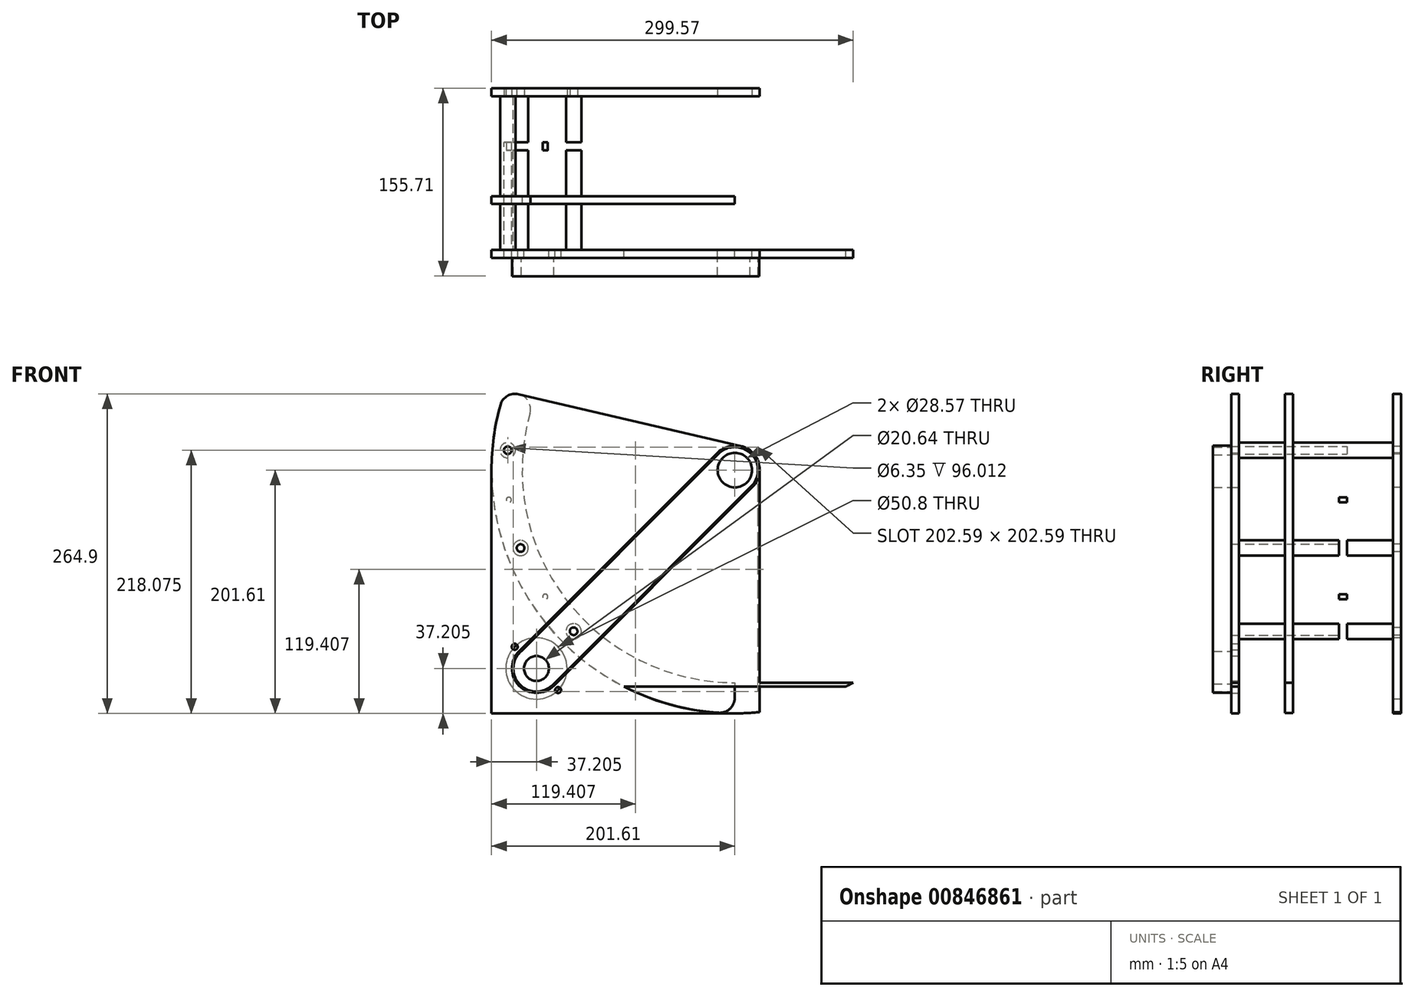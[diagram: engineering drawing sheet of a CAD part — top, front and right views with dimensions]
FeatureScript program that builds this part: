
annotation { "Feature Type Name" : "Feature", "Feature Type Description" : "" }
export const myFeature = defineFeature(function(context is Context, id is Id, definition is map)
    precondition{}
    {
        {
            var Q0;
            Q0=qCreatedBy(makeId("Front.planeOp"),FACE);
            var sketch = newSketch(context, id + "F0", { "sketchPlane" : qUnion([Q0])});
            skCircle(sketch, "E0", {"center": v(0, 0) * mm, "radius": 61.91 * mm});
            skCircle(sketch, "E1", {"center": v(0, 0) * mm, "radius": 176.21 * mm});
            skCircle(sketch, "E2.cCircle", {"center": v(0, 0) * mm, "radius": 6.35 * mm, "construction": true});
            skLineSegment(sketch, "E2.0", {"start": v(-3.67, 6.35) * mm, "end": v(3.67, 6.35) * mm});
            skLineSegment(sketch, "E2.1", {"start": v(3.67, 6.35) * mm, "end": v(7.33, 0) * mm});
            skLineSegment(sketch, "E2.2", {"start": v(7.33, 0) * mm, "end": v(3.67, -6.35) * mm});
            skLineSegment(sketch, "E2.3", {"start": v(3.67, -6.35) * mm, "end": v(-3.67, -6.35) * mm});
            skLineSegment(sketch, "E2.4", {"start": v(-3.67, -6.35) * mm, "end": v(-7.33, 0) * mm});
            skLineSegment(sketch, "E2.5", {"start": v(-7.33, 0) * mm, "end": v(-3.67, 6.35) * mm});
            skPoint(sketch, "E2.0.midPoint", {"position": v(0, 6.35) * mm});
            skCircle(sketch, "E3", {"center": v(0, 0) * mm, "radius": 201.61 * mm});
            skLineSegment(sketch, "E4", {"start": v(0, -176.21) * mm, "end": v(267.79, -176.21) * mm});
            skCircle(sketch, "E5", {"center": v(0, 0) * mm, "radius": 188.91 * mm, "construction": true});
            skCircle(sketch, "E6", {"center": v(-133.58, -133.58) * mm, "radius": 3.18 * mm});
            skLineSegment(sketch, "E7", {"start": v(0, 0) * mm, "end": v(-133.58, -133.58) * mm, "construction": true});
            skLineSegment(sketch, "E8", {"start": v(0, 0) * mm, "end": v(-190.63, 65.64) * mm});
            skCircle(sketch, "E9.1.0", {"center": v(-177.52, -64.61) * mm, "radius": 3.18 * mm});
            skCircle(sketch, "E9.2.0", {"center": v(-188.2, 16.46) * mm, "radius": 3.18 * mm});
            skCircle(sketch, "E9.3.0", {"center": v(-163.6, 94.46) * mm, "radius": 3.18 * mm});
            skLineSegment(sketch, "E9.anchor2", {"start": v(0, 0) * mm, "end": v(-163.6, 94.46) * mm, "construction": true});
            skLineSegment(sketch, "E10", {"start": v(267.83, -179.39) * mm, "end": v(-92.02, -179.39) * mm});
            skLineSegment(sketch, "E11", {"start": v(267.79, -176.21) * mm, "end": v(267.83, -179.39) * mm});
            skCircle(sketch, "E12", {"center": v(0, 0) * mm, "radius": 14.29 * mm});
            skCircle(sketch, "E13", {"center": v(0, 0) * mm, "radius": 20.64 * mm});
            skLineSegment(sketch, "E14", {"start": v(4.69, 20.1) * mm, "end": v(-190.63, 65.64) * mm});
            skLineSegment(sketch, "E15", {"start": v(20.64, 0) * mm, "end": v(20.64, -176.21) * mm});
            skLineSegment(sketch, "E16", {"start": v(20.64, -175.98) * mm, "end": v(20.64, -200.55) * mm});
            skLineSegment(sketch, "E17", {"start": v(-201.61, 0) * mm, "end": v(-201.61, -201.61) * mm});
            skLineSegment(sketch, "E18", {"start": v(-201.61, -201.61) * mm, "end": v(0, -201.61) * mm});
            skCircle(sketch, "E19", {"center": v(-164.4, -164.4) * mm, "radius": 10.32 * mm});
            skCircle(sketch, "E20", {"center": v(-146.44, -182.37) * mm, "radius": 2.49 * mm});
            skCircle(sketch, "E21", {"center": v(-182.37, -146.44) * mm, "radius": 2.49 * mm});
            skCircle(sketch, "E22", {"center": v(-164.4, -164.4) * mm, "radius": 25.4 * mm, "construction": true});
            skLineSegment(sketch, "E23", {"start": v(-146.44, -182.37) * mm, "end": v(-182.37, -146.44) * mm, "construction": true});
            skCircle(sketch, "E24", {"center": v(-164.4, -164.4) * mm, "radius": 19.1 * mm});
            skCircle(sketch, "E25", {"center": v(0, 0) * mm, "radius": 19.1 * mm});
            skLineSegment(sketch, "E26", {"start": v(-201.61, -201.61) * mm, "end": v(-133.58, -133.58) * mm, "construction": true});
            skSolve(sketch);
        }
        {
            var Q0;
            {var subQ0=sQuery(id+"F0.wireOp",EDGE,"E8");var subQ1=sQuery(id+"F0.wireOp",EDGE,"E0");var subQ2=makeQuery(id+"F0.imprint","INTERSECT",VERTEX,{"derivedFrom":[subQ1,subQ0]});Q0=makeQuery(id+"F0.imprint","IMPRINT",FACE,{"disambiguationData":[TD([[makeQuery(id+"F0.imprint","IMPRINT",EDGE,{"disambiguationData":[TD([[subQ2,1.0]])],"derivedFrom":subQ1}),1.0]])]});}
            var Q1;
            {var subQ0=sQuery(id+"F0.wireOp",EDGE,"E8");var subQ1=sQuery(id+"F0.wireOp",EDGE,"E0");var subQ2=makeQuery(id+"F0.imprint","INTERSECT",VERTEX,{"derivedFrom":[subQ1,subQ0]});Q1=makeQuery(id+"F0.imprint","IMPRINT",FACE,{"disambiguationData":[TD([[makeQuery(id+"F0.imprint","IMPRINT",EDGE,{"disambiguationData":[TD([[subQ2,1.0]])],"derivedFrom":subQ1}),-1.0]])]});}
            var Q2;
            {var subQ0=sQuery(id+"F0.wireOp",EDGE,"E8");var subQ1=sQuery(id+"F0.wireOp",EDGE,"E0");var subQ2=makeQuery(id+"F0.imprint","INTERSECT",VERTEX,{"derivedFrom":[subQ1,subQ0]});Q2=makeQuery(id+"F0.imprint","IMPRINT",FACE,{"disambiguationData":[TD([[makeQuery(id+"F0.imprint","IMPRINT",EDGE,{"disambiguationData":[TD([[subQ2,-1.0]])],"derivedFrom":subQ1}),-1.0]])]});}
            var Q3;
            {var subQ0=sQuery(id+"F0.wireOp",EDGE,"E8");var subQ1=sQuery(id+"F0.wireOp",EDGE,"E1");var subQ2=makeQuery(id+"F0.imprint","INTERSECT",VERTEX,{"derivedFrom":[subQ1,subQ0]});Q3=makeQuery(id+"F0.imprint","IMPRINT",FACE,{"disambiguationData":[TD([[makeQuery(id+"F0.imprint","IMPRINT",EDGE,{"disambiguationData":[TD([[subQ2,1.0]])],"derivedFrom":subQ1}),-1.0]])]});}
            var Q4;
            Q4=makeQuery(id+"F0.imprint","IMPRINT",FACE,{"disambiguationData":[TD([[makeQuery(id+"F0.imprint","IMPRINT",EDGE,{"derivedFrom":sQuery(id+"F0.wireOp",EDGE,"E12")}),-1.0]])]});
            var Q5;
            {var subQ0=sQuery(id+"F0.wireOp",EDGE,"E8");var subQ1=sQuery(id+"F0.wireOp",EDGE,"E0");var subQ2=makeQuery(id+"F0.imprint","INTERSECT",VERTEX,{"derivedFrom":[subQ1,subQ0]});Q5=makeQuery(id+"F0.imprint","IMPRINT",FACE,{"disambiguationData":[TD([[makeQuery(id+"F0.imprint","IMPRINT",EDGE,{"disambiguationData":[TD([[subQ2,-1.0]])],"derivedFrom":subQ1}),1.0]])]});}
            var Q6;
            {var subQ0=sQuery(id+"F0.wireOp",EDGE,"E4");var subQ1=sQuery(id+"F0.wireOp",EDGE,"E1");var subQ2=makeQuery(id+"F0.imprint","INTERSECT",VERTEX,{"derivedFrom":[subQ1,subQ0]});Q6=makeQuery(id+"F0.imprint","IMPRINT",FACE,{"disambiguationData":[TD([[makeQuery(id+"F0.imprint","IMPRINT",EDGE,{"disambiguationData":[TD([[subQ2,-1.0]])],"derivedFrom":subQ1}),-1.0]])]});}
            var Q7;
            {var subQ0=sQuery(id+"F0.wireOp",EDGE,"E10");var subQ1=sQuery(id+"F0.wireOp",EDGE,"E3");var subQ2=makeQuery(id+"F0.imprint","INTERSECT",VERTEX,{"disambiguationData":[OD(0.0)],"derivedFrom":[subQ1,subQ0]});Q7=makeQuery(id+"F0.imprint","IMPRINT",FACE,{"disambiguationData":[TD([[makeQuery(id+"F0.imprint","IMPRINT",EDGE,{"disambiguationData":[TD([[subQ2,-1.0]])],"derivedFrom":subQ1}),1.0]])]});}
            var Q8;
            Q8=makeQuery(id+"F0.imprint","IMPRINT",FACE,{"disambiguationData":[TD([[makeQuery(id+"F0.imprint","IMPRINT",EDGE,{"derivedFrom":sQuery(id+"F0.wireOp",EDGE,"E6")}),-1.0]])]});
            var Q9;
            Q9=makeQuery(id+"F0.imprint","IMPRINT",FACE,{"disambiguationData":[TD([[makeQuery(id+"F0.imprint","IMPRINT",EDGE,{"derivedFrom":sQuery(id+"F0.wireOp",EDGE,"E25")}),-1.0]])]});
            var Q10;
            {var subQ3=sQuery(id+"F0.wireOp",EDGE,"E17");Q10=makeQuery(id+"F0.imprint","IMPRINT",FACE,{"disambiguationData":[TD([[makeQuery(id+"F0.imprint","IMPRINT",EDGE,{"derivedFrom":subQ3}),1.0]])]});}
            var Q11;
            Q11=makeQuery(id+"F0.imprint","IMPRINT",FACE,{"disambiguationData":[TD([[makeQuery(id+"F0.imprint","IMPRINT",EDGE,{"derivedFrom":sQuery(id+"F0.wireOp",EDGE,"E19")}),-1.0]])]});
            extrude(context, id + "F1", {"entities" : qUnion([Q0, Q1, Q2, Q3, Q4, Q5, Q6, Q7, Q8, Q9, Q10, Q11]), "depth" : 6.6 * mm, "offsetDistance" : 25.4 * mm});
        }
        {
            var Q0;
            Q0=makeQuery(id+"F1.opExtrude","CAP_FACE",FACE,{"disambiguationData":[OSD([sQuery(id+"F0.wireOp",EDGE,"E1"),sQuery(id+"F0.wireOp",EDGE,"E3"),sQuery(id+"F0.wireOp",EDGE,"E4"),sQuery(id+"F0.wireOp",EDGE,"E6"),sQuery(id+"F0.wireOp",EDGE,"E8"),sQuery(id+"F0.wireOp",EDGE,"E9.1.0"),sQuery(id+"F0.wireOp",EDGE,"E9.2.0"),sQuery(id+"F0.wireOp",EDGE,"E9.3.0"),sQuery(id+"F0.wireOp",EDGE,"E10")])],"isStart":true});
            var sketch = newSketch(context, id + "F2", { "sketchPlane" : qUnion([Q0])});
            skCircle(sketch, "E27", {"center": v(188.2, 16.46) * mm, "radius": 6.35 * mm});
            skCircle(sketch, "E28", {"center": v(177.52, -64.61) * mm, "radius": 6.35 * mm});
            skCircle(sketch, "E29", {"center": v(133.58, -133.58) * mm, "radius": 6.35 * mm});
            skSolve(sketch);
        }
        {
            var Q0;
            Q0=makeQuery(id+"F2.imprint","IMPRINT",FACE,{"disambiguationData":[TD([[makeQuery(id+"F2.imprint","IMPRINT",EDGE,{"derivedFrom":sQuery(id+"F2.wireOp",EDGE,"E27")}),1.0]])]});
            var Q1;
            Q1=makeQuery(id+"F2.imprint","IMPRINT",FACE,{"disambiguationData":[TD([[makeQuery(id+"F2.imprint","IMPRINT",EDGE,{"derivedFrom":sQuery(id+"F2.wireOp",EDGE,"E28")}),1.0]])]});
            var Q2;
            Q2=makeQuery(id+"F2.imprint","IMPRINT",FACE,{"disambiguationData":[TD([[makeQuery(id+"F2.imprint","IMPRINT",EDGE,{"derivedFrom":sQuery(id+"F2.wireOp",EDGE,"E29")}),1.0]])]});
            extrude(context, id + "F3", {"entities" : qUnion([Q0, Q1, Q2]), "operationType" : NewBodyOperationType.ADD, "depth" : 38.1 * mm, "offsetDistance" : 25.4 * mm});
        }
        {
            var Q0;
            Q0=makeQuery(id+"F3.opExtrude","CAP_FACE",FACE,{"disambiguationData":[OSD([sQuery(id+"F0.wireOp",EDGE,"E6"),sQuery(id+"F2.wireOp",EDGE,"E29")])],"isStart":false});
            var sketch = newSketch(context, id + "F4", { "sketchPlane" : qUnion([Q0])});
            skCircle(sketch, "E30", {"center": v(0, 0) * mm, "radius": 201.61 * mm});
            skCircle(sketch, "E31", {"center": v(0, 0) * mm, "radius": 176.21 * mm});
            skLineSegment(sketch, "E32", {"start": v(133.58, 133.58) * mm, "end": v(0, 0) * mm, "construction": true});
            skCircle(sketch, "E33", {"center": v(0, 0) * mm, "radius": 188.91 * mm, "construction": true});
            skCircle(sketch, "E34.1.0", {"center": v(178.89, 60.72) * mm, "radius": 6.35 * mm});
            skCircle(sketch, "E34.2.0", {"center": v(187.3, -24.66) * mm, "radius": 6.35 * mm});
            skCircle(sketch, "E34.3.0", {"center": v(157.08, -104.95) * mm, "radius": 6.35 * mm});
            skCircle(sketch, "E34.4.0", {"center": v(94.46, -163.6) * mm, "radius": 6.35 * mm});
            skLineSegment(sketch, "E34.anchor1", {"start": v(0, 0) * mm, "end": v(133.58, 133.58) * mm, "construction": true});
            skLineSegment(sketch, "E34.anchor2", {"start": v(0, 0) * mm, "end": v(94.46, -163.6) * mm, "construction": true});
            skLineSegment(sketch, "E35.0", {"start": v(-4.69, 20.1) * mm, "end": v(190.63, 65.64) * mm});
            skCircle(sketch, "E36", {"center": v(178.89, 60.72) * mm, "radius": 3.18 * mm});
            skCircle(sketch, "E37", {"center": v(188.2, 16.46) * mm, "radius": 3.18 * mm});
            skCircle(sketch, "E38", {"center": v(187.3, -24.66) * mm, "radius": 3.18 * mm});
            skCircle(sketch, "E39", {"center": v(177.52, -64.61) * mm, "radius": 3.18 * mm});
            skCircle(sketch, "E40", {"center": v(157.08, -104.95) * mm, "radius": 3.18 * mm});
            skCircle(sketch, "E41", {"center": v(133.58, -133.58) * mm, "radius": 3.18 * mm});
            skLineSegment(sketch, "E42", {"start": v(0, 0) * mm, "end": v(0, -201.61) * mm});
            skSolve(sketch);
        }
        {
            var Q0;
            Q0=makeQuery(id+"F4.imprint","IMPRINT",FACE,{"disambiguationData":[TD([[makeQuery(id+"F4.imprint","IMPRINT",EDGE,{"derivedFrom":sQuery(id+"F4.wireOp",EDGE,"E34.2.0")}),-1.0]])]});
            var Q1;
            Q1=makeQuery(id+"F4.imprint","IMPRINT",FACE,{"disambiguationData":[TD([[makeQuery(id+"F4.imprint","IMPRINT",EDGE,{"derivedFrom":sQuery(id+"F4.wireOp",EDGE,"E41")}),1.0]])]});
            var Q2;
            {var subQ0=sQuery(id+"F4.wireOp",EDGE,"E35.0");var subQ1=sQuery(id+"F4.wireOp",EDGE,"E34.1.0");var subQ2=makeQuery(id+"F4.imprint","INTERSECT",VERTEX,{"disambiguationData":[OD(0.0)],"derivedFrom":[subQ1,subQ0]});Q2=makeQuery(id+"F4.imprint","IMPRINT",FACE,{"disambiguationData":[TD([[makeQuery(id+"F4.imprint","IMPRINT",EDGE,{"disambiguationData":[TD([[subQ2,-1.0]])],"derivedFrom":subQ1}),1.0]])]});}
            var Q3;
            {var subQ0=sQuery(id+"F4.wireOp",EDGE,"E36");var subQ1=sQuery(id+"F4.wireOp",EDGE,"E35.0");var subQ2=makeQuery(id+"F4.imprint","INTERSECT",VERTEX,{"disambiguationData":[OD(0.0)],"derivedFrom":[subQ1,subQ0]});Q3=makeQuery(id+"F4.imprint","IMPRINT",FACE,{"disambiguationData":[TD([[makeQuery(id+"F4.imprint","IMPRINT",EDGE,{"disambiguationData":[TD([[subQ2,-1.0]])],"derivedFrom":subQ1}),-1.0]])]});}
            var Q4;
            Q4=makeQuery(id+"F4.imprint","IMPRINT",FACE,{"disambiguationData":[TD([[makeQuery(id+"F4.imprint","IMPRINT",EDGE,{"derivedFrom":sQuery(id+"F4.wireOp",EDGE,"E34.4.0")}),1.0]])]});
            var Q5;
            Q5=makeQuery(id+"F4.imprint","IMPRINT",FACE,{"disambiguationData":[TD([[makeQuery(id+"F4.imprint","IMPRINT",EDGE,{"derivedFrom":sQuery(id+"F4.wireOp",EDGE,"E34.3.0")}),1.0]])]});
            var Q6;
            Q6=makeQuery(id+"F4.imprint","IMPRINT",FACE,{"disambiguationData":[TD([[makeQuery(id+"F4.imprint","IMPRINT",EDGE,{"derivedFrom":sQuery(id+"F4.wireOp",EDGE,"E40")}),1.0]])]});
            var Q7;
            Q7=makeQuery(id+"F4.imprint","IMPRINT",FACE,{"disambiguationData":[TD([[makeQuery(id+"F4.imprint","IMPRINT",EDGE,{"derivedFrom":sQuery(id+"F4.wireOp",EDGE,"E34.2.0")}),1.0]])]});
            var Q8;
            Q8=makeQuery(id+"F4.imprint","IMPRINT",FACE,{"disambiguationData":[TD([[makeQuery(id+"F4.imprint","IMPRINT",EDGE,{"derivedFrom":sQuery(id+"F4.wireOp",EDGE,"E38")}),1.0]])]});
            extrude(context, id + "F5", {"entities" : qUnion([Q0, Q1, Q2, Q3, Q4, Q5, Q6, Q7, Q8]), "operationType" : NewBodyOperationType.ADD, "depth" : 6.6 * mm, "offsetDistance" : 25.4 * mm});
        }
        {
            var Q0;
            Q0=makeQuery(id+"F5.opExtrude","CAP_FACE",FACE,{"disambiguationData":[OSD([sQuery(id+"F4.wireOp",EDGE,"E30"),sQuery(id+"F4.wireOp",EDGE,"E31"),sQuery(id+"F4.wireOp",EDGE,"E35.0"),sQuery(id+"F4.wireOp",EDGE,"8neH0s6F-ErBh-p7Tc-FeBG-JO8hClFv3z9E"),sQuery(id+"F4.wireOp",EDGE,"E36"),sQuery(id+"F4.wireOp",EDGE,"E37"),sQuery(id+"F4.wireOp",EDGE,"E38"),sQuery(id+"F4.wireOp",EDGE,"E39"),sQuery(id+"F4.wireOp",EDGE,"E40"),sQuery(id+"F4.wireOp",EDGE,"E41"),sQuery(id+"F4.wireOp",EDGE,"E42")])],"isStart":false});
            var sketch = newSketch(context, id + "F6", { "sketchPlane" : qUnion([Q0])});
            skCircle(sketch, "E43", {"center": v(178.89, 60.72) * mm, "radius": 6.35 * mm});
            skCircle(sketch, "E44", {"center": v(187.3, -24.66) * mm, "radius": 6.35 * mm});
            skCircle(sketch, "E45", {"center": v(157.08, -104.95) * mm, "radius": 6.35 * mm});
            skCircle(sketch, "E46", {"center": v(188.2, 16.46) * mm, "radius": 6.35 * mm});
            skCircle(sketch, "E47", {"center": v(177.52, -64.61) * mm, "radius": 6.35 * mm});
            skCircle(sketch, "E48", {"center": v(133.58, -133.58) * mm, "radius": 6.35 * mm});
            skSolve(sketch);
        }
        {
            var Q0;
            Q0=makeQuery(id+"F6.imprint","IMPRINT",FACE,{"disambiguationData":[TD([[makeQuery(id+"F6.imprint","IMPRINT",EDGE,{"derivedFrom":sQuery(id+"F6.wireOp",EDGE,"E46")}),1.0]])]});
            var Q1;
            Q1=makeQuery(id+"F6.imprint","IMPRINT",FACE,{"disambiguationData":[TD([[makeQuery(id+"F6.imprint","IMPRINT",EDGE,{"derivedFrom":sQuery(id+"F6.wireOp",EDGE,"E47")}),1.0]])]});
            var Q2;
            Q2=makeQuery(id+"F6.imprint","IMPRINT",FACE,{"disambiguationData":[TD([[makeQuery(id+"F6.imprint","IMPRINT",EDGE,{"derivedFrom":sQuery(id+"F6.wireOp",EDGE,"E48")}),1.0]])]});
            extrude(context, id + "F7", {"entities" : qUnion([Q0, Q1, Q2]), "operationType" : NewBodyOperationType.ADD, "depth" : 38.1 * mm, "offsetDistance" : 25.4 * mm});
        }
        {
            var Q0;
            Q0=makeQuery(id+"F7.opExtrude","CAP_FACE",FACE,{"disambiguationData":[OSD([sQuery(id+"F4.wireOp",EDGE,"E37"),sQuery(id+"F6.wireOp",EDGE,"E46")])],"isStart":false});
            var sketch = newSketch(context, id + "F8", { "sketchPlane" : qUnion([Q0])});
            skCircle(sketch, "E49.0", {"center": v(163.6, 94.46) * mm, "radius": 2.15 * mm});
            skArc(sketch, "E50.1", {"start": v(0, -176.21) * mm, "mid": v(144.21, -101.26) * mm, "end": v(165.74, 59.84) * mm});
            skPoint(sketch, "E51.0", {"position": v(178.19, 62.74) * mm});
            skLineSegment(sketch, "E52.0", {"start": v(165.74, 59.84) * mm, "end": v(190.63, 65.64) * mm});
            skLineSegment(sketch, "E53.0.0", {"start": v(190.63, 65.64) * mm, "end": v(165.74, 59.84) * mm});
            skArc(sketch, "E53.0.1", {"start": v(165.74, 59.84) * mm, "mid": v(144.21, -101.26) * mm, "end": v(0, -176.21) * mm});
            skLineSegment(sketch, "E53.0.2", {"start": v(0, -176.21) * mm, "end": v(0, -201.61) * mm});
            skArc(sketch, "E53.0.3", {"start": v(0, -201.61) * mm, "mid": v(164.14, -117.08) * mm, "end": v(190.63, 65.64) * mm});
            skCircle(sketch, "E54.0", {"center": v(188.2, 16.46) * mm, "radius": 2.15 * mm});
            skCircle(sketch, "E55.0", {"center": v(177.52, -64.61) * mm, "radius": 2.15 * mm});
            skCircle(sketch, "E56.0", {"center": v(133.58, -133.58) * mm, "radius": 2.15 * mm});
            skCircle(sketch, "E57.0", {"center": v(157.08, -104.95) * mm, "radius": 2.15 * mm});
            skCircle(sketch, "E58.0", {"center": v(187.3, -24.66) * mm, "radius": 2.15 * mm});
            skCircle(sketch, "E59.0", {"center": v(178.89, 60.72) * mm, "radius": 2.15 * mm});
            skSolve(sketch);
        }
        {
            var Q0;
            {var subQ5=sQuery(id+"F8.wireOp",EDGE,"E53.0.1");Q0=makeQuery(id+"F8.imprint","IMPRINT",FACE,{"disambiguationData":[TD([[makeQuery(id+"F8.imprint","IMPRINT",EDGE,{"derivedFrom":subQ5}),1.0]])]});}
            var Q1;
            {var subQ0=sQuery(id+"F8.wireOp",EDGE,"E59.0");var subQ1=sQuery(id+"F8.wireOp",EDGE,"E53.0.0");var subQ2=makeQuery(id+"F8.imprint","INTERSECT",VERTEX,{"disambiguationData":[OD(0.0)],"derivedFrom":[subQ1,subQ0]});Q1=makeQuery(id+"F8.imprint","IMPRINT",FACE,{"disambiguationData":[TD([[makeQuery(id+"F8.imprint","IMPRINT",EDGE,{"disambiguationData":[TD([[subQ2,-1.0]])],"derivedFrom":subQ1}),1.0]])]});}
            var Q2;
            Q2=makeQuery(id+"F8.imprint","IMPRINT",FACE,{"disambiguationData":[TD([[makeQuery(id+"F8.imprint","IMPRINT",EDGE,{"derivedFrom":makeQuery(id+"F7.opExtrude","CAP_EDGE",EDGE,{"disambiguationData":[OSD([sQuery(id+"F6.wireOp",EDGE,"E46")])],"isStart":false})}),1.0]])]});
            var Q3;
            Q3=makeQuery(id+"F8.imprint","IMPRINT",FACE,{"disambiguationData":[TD([[makeQuery(id+"F8.imprint","IMPRINT",EDGE,{"derivedFrom":sQuery(id+"F8.wireOp",EDGE,"E58.0")}),1.0]])]});
            var Q4;
            Q4=makeQuery(id+"F8.imprint","IMPRINT",FACE,{"disambiguationData":[TD([[makeQuery(id+"F8.imprint","IMPRINT",EDGE,{"derivedFrom":sQuery(id+"F8.wireOp",EDGE,"E57.0")}),1.0]])]});
            extrude(context, id + "F9", {"entities" : qUnion([Q0, Q1, Q2, Q3, Q4]), "operationType" : NewBodyOperationType.ADD, "depth" : 6.6 * mm, "offsetDistance" : 25.4 * mm});
        }
        {
            var Q0;
            Q0=makeQuery(id+"F9.opExtrude","CAP_FACE",FACE,{"disambiguationData":[OSD([sQuery(id+"F8.wireOp",EDGE,"E49.0"),sQuery(id+"F8.wireOp",EDGE,"E53.0.0"),sQuery(id+"F8.wireOp",EDGE,"E53.0.1"),sQuery(id+"F8.wireOp",EDGE,"E53.0.2"),sQuery(id+"F8.wireOp",EDGE,"E53.0.3"),sQuery(id+"F8.wireOp",EDGE,"E54.0"),sQuery(id+"F8.wireOp",EDGE,"E55.0"),sQuery(id+"F8.wireOp",EDGE,"E56.0"),sQuery(id+"F8.wireOp",EDGE,"E57.0"),sQuery(id+"F8.wireOp",EDGE,"E58.0"),sQuery(id+"F8.wireOp",EDGE,"E59.0")])],"isStart":false});
            var sketch = newSketch(context, id + "F10", { "sketchPlane" : qUnion([Q0])});
            skCircle(sketch, "E60.0", {"center": v(163.6, 94.46) * mm, "radius": 6.35 * mm});
            skCircle(sketch, "E61.0", {"center": v(188.2, 16.46) * mm, "radius": 6.35 * mm});
            skCircle(sketch, "E62.1", {"center": v(177.52, -64.61) * mm, "radius": 6.35 * mm});
            skCircle(sketch, "E63.0", {"center": v(133.58, -133.58) * mm, "radius": 6.35 * mm});
            skCircle(sketch, "E64", {"center": v(178.89, 60.72) * mm, "radius": 6.35 * mm});
            skCircle(sketch, "E65", {"center": v(187.3, -24.66) * mm, "radius": 6.35 * mm});
            skCircle(sketch, "E66", {"center": v(157.08, -104.95) * mm, "radius": 6.35 * mm});
            skSolve(sketch);
        }
        {
            var Q0;
            Q0=makeQuery(id+"F10.imprint","IMPRINT",FACE,{"disambiguationData":[TD([[makeQuery(id+"F10.imprint","IMPRINT",EDGE,{"derivedFrom":sQuery(id+"F10.wireOp",EDGE,"E61.0")}),1.0]])]});
            var Q1;
            Q1=makeQuery(id+"F10.imprint","IMPRINT",FACE,{"disambiguationData":[TD([[makeQuery(id+"F10.imprint","IMPRINT",EDGE,{"derivedFrom":sQuery(id+"F10.wireOp",EDGE,"E62.1")}),1.0]])]});
            var Q2;
            Q2=makeQuery(id+"F10.imprint","IMPRINT",FACE,{"disambiguationData":[TD([[makeQuery(id+"F10.imprint","IMPRINT",EDGE,{"derivedFrom":sQuery(id+"F10.wireOp",EDGE,"E63.0")}),1.0]])]});
            extrude(context, id + "F11", {"entities" : qUnion([Q0, Q1, Q2]), "operationType" : NewBodyOperationType.ADD, "depth" : 38.1 * mm, "offsetDistance" : 25.4 * mm});
        }
        {
            var Q0;
            Q0=makeQuery(id+"F11.opExtrude","CAP_FACE",FACE,{"disambiguationData":[OSD([sQuery(id+"F4.wireOp",EDGE,"E37"),sQuery(id+"F10.wireOp",EDGE,"E61.0")])],"isStart":false});
            var sketch = newSketch(context, id + "F12", { "sketchPlane" : qUnion([Q0])});
            skLineSegment(sketch, "E67.0", {"start": v(-4.69, 20.1) * mm, "end": v(190.63, 65.64) * mm});
            skArc(sketch, "E68.0", {"start": v(-20.64, 0) * mm, "mid": v(-16.17, 12.83) * mm, "end": v(-4.69, 20.1) * mm});
            skLineSegment(sketch, "E69.0", {"start": v(-20.64, 0) * mm, "end": v(-20.64, -176.21) * mm});
            skCircle(sketch, "E70.0", {"center": v(0, 0) * mm, "radius": 14.29 * mm});
            skCircle(sketch, "E71.0", {"center": v(163.6, 94.46) * mm, "radius": 3.18 * mm});
            skCircle(sketch, "E72.0", {"center": v(188.2, 16.46) * mm, "radius": 3.18 * mm});
            skCircle(sketch, "E73.0", {"center": v(177.52, -64.61) * mm, "radius": 3.18 * mm});
            skCircle(sketch, "E74.0", {"center": v(133.58, -133.58) * mm, "radius": 3.18 * mm});
            skLineSegment(sketch, "E75.0", {"start": v(-20.64, -176.21) * mm, "end": v(-20.64, -176.21) * mm});
            skLineSegment(sketch, "E76", {"start": v(-20.64, -176.21) * mm, "end": v(-20.64, -200.55) * mm});
            skLineSegment(sketch, "E77.0", {"start": v(201.61, 0) * mm, "end": v(201.61, -201.61) * mm});
            skLineSegment(sketch, "E78.0", {"start": v(201.61, -201.61) * mm, "end": v(0, -201.61) * mm});
            skArc(sketch, "E79.0", {"start": v(0, -201.61) * mm, "mid": v(-10.33, -201.35) * mm, "end": v(-20.64, -200.55) * mm});
            skArc(sketch, "E80.0", {"start": v(190.63, 65.64) * mm, "mid": v(198.85, 33.28) * mm, "end": v(201.61, 0) * mm});
            skCircle(sketch, "E81.0", {"center": v(164.4, -164.4) * mm, "radius": 10.32 * mm});
            skCircle(sketch, "E82", {"center": v(164.4, -164.4) * mm, "radius": 25.4 * mm});
            skSolve(sketch);
        }
        {
            var Q0;
            Q0=makeQuery(id+"F12.imprint","IMPRINT",FACE,{"disambiguationData":[TD([[makeQuery(id+"F12.imprint","IMPRINT",EDGE,{"derivedFrom":sQuery(id+"F12.wireOp",EDGE,"E67.0")}),-1.0]])]});
            var Q1;
            Q1=makeQuery(id+"F12.imprint","IMPRINT",FACE,{"disambiguationData":[TD([[makeQuery(id+"F12.imprint","IMPRINT",EDGE,{"derivedFrom":sQuery(id+"F12.wireOp",EDGE,"E72.0")}),-1.0]])]});
            extrude(context, id + "F13", {"entities" : qUnion([Q0, Q1]), "operationType" : NewBodyOperationType.ADD, "depth" : 6.6 * mm, "offsetDistance" : 25.4 * mm});
        }
        {
            var Q0;
            Q0=makeQuery(id+"F1.opExtrude","SWEPT_EDGE",EDGE,{"disambiguationData":[OSD([sQuery(id+"F0.wireOp",EDGE,"E3"),sQuery(id+"F0.wireOp",EDGE,"E8"),sQuery(id+"F0.wireOp",EDGE,"E14")])]});
            var Q1;
            Q1=makeQuery(id+"F5.opExtrude","SWEPT_EDGE",EDGE,{"disambiguationData":[OSD([sQuery(id+"F4.wireOp",EDGE,"E30"),sQuery(id+"F4.wireOp",EDGE,"E35.0")])]});
            var Q2;
            Q2=makeQuery(id+"F9.opExtrude","SWEPT_EDGE",EDGE,{"disambiguationData":[OSD([sQuery(id+"F8.wireOp",EDGE,"E53.0.0"),sQuery(id+"F8.wireOp",EDGE,"E53.0.1")])]});
            var Q3;
            Q3=makeQuery(id+"F9.opExtrude","SWEPT_EDGE",EDGE,{"disambiguationData":[OSD([sQuery(id+"F8.wireOp",EDGE,"E53.0.0"),sQuery(id+"F8.wireOp",EDGE,"E53.0.3")])]});
            var Q4;
            Q4=makeQuery(id+"F5.opExtrude","SWEPT_EDGE",EDGE,{"disambiguationData":[OSD([sQuery(id+"F4.wireOp",EDGE,"E31"),sQuery(id+"F4.wireOp",EDGE,"E35.0")])]});
            var Q5;
            Q5=makeQuery(id+"F13.opExtrude","SWEPT_EDGE",EDGE,{"disambiguationData":[OSD([sQuery(id+"F12.wireOp",EDGE,"E67.0"),sQuery(id+"F12.wireOp",EDGE,"E80.0")])]});
            var Q6;
            Q6=makeQuery(id+"F5.opExtrude","SWEPT_EDGE",EDGE,{"disambiguationData":[OSD([sQuery(id+"F4.wireOp",EDGE,"E30"),sQuery(id+"F4.wireOp",EDGE,"E42")])]});
            var Q7;
            Q7=makeQuery(id+"F9.opExtrude","SWEPT_EDGE",EDGE,{"disambiguationData":[OSD([sQuery(id+"F8.wireOp",EDGE,"E53.0.2"),sQuery(id+"F8.wireOp",EDGE,"E53.0.3")])]});
            fillet(context, id + "F14", {"entities" : qUnion([Q0, Q1, Q2, Q3, Q4, Q5, Q6, Q7]), "radius" : 12.7 * mm, "tangentPropagation" : true, "allowEdgeOverflow" : false});
        }
        {
            var Q0;
            Q0=makeQuery(id+"F1.opExtrude","CAP_FACE",FACE,{"disambiguationData":[OSD([sQuery(id+"F0.wireOp",EDGE,"E3"),sQuery(id+"F0.wireOp",EDGE,"E4"),sQuery(id+"F0.wireOp",EDGE,"E6"),sQuery(id+"F0.wireOp",EDGE,"E9.1.0"),sQuery(id+"F0.wireOp",EDGE,"E9.2.0"),sQuery(id+"F0.wireOp",EDGE,"E9.3.0"),sQuery(id+"F0.wireOp",EDGE,"E12"),sQuery(id+"F0.wireOp",EDGE,"E13"),sQuery(id+"F0.wireOp",EDGE,"E14"),sQuery(id+"F0.wireOp",EDGE,"E15"),sQuery(id+"F0.wireOp",EDGE,"E16"),sQuery(id+"F0.wireOp",EDGE,"E17"),sQuery(id+"F0.wireOp",EDGE,"E18"),sQuery(id+"F0.wireOp",EDGE,"E19"),sQuery(id+"F0.wireOp",EDGE,"E20"),sQuery(id+"F0.wireOp",EDGE,"E21")])],"isStart":false});
            var sketch = newSketch(context, id + "F15", { "sketchPlane" : qUnion([Q0])});
            skCircle(sketch, "E83.0", {"center": v(0, 0) * mm, "radius": 19.1 * mm});
            skCircle(sketch, "E84.0", {"center": v(-164.4, -164.4) * mm, "radius": 19.1 * mm});
            skCircle(sketch, "E85", {"center": v(-164.4, -164.4) * mm, "radius": 20.24 * mm});
            skCircle(sketch, "E86", {"center": v(0, 0) * mm, "radius": 20.24 * mm});
            skLineSegment(sketch, "E87", {"start": v(-178.72, -150.1) * mm, "end": v(-14.31, 14.31) * mm});
            skLineSegment(sketch, "E88", {"start": v(-177.05, -150.1) * mm, "end": v(-14.31, 12.65) * mm});
            skLineSegment(sketch, "E89.MirrorCS", {"start": v(-150.1, -178.72) * mm, "end": v(14.31, -14.31) * mm});
            skLineSegment(sketch, "E90.MirrorCS", {"start": v(-150.1, -177.05) * mm, "end": v(12.65, -14.31) * mm});
            skSolve(sketch);
        }
        {
            var Q0;
            Q0=qSketchRegion(id+"F15",true);
            extrude(context, id + "F16", {"entities" : qUnion([Q0]), "depth" : 15 * mm});
        }
    });
